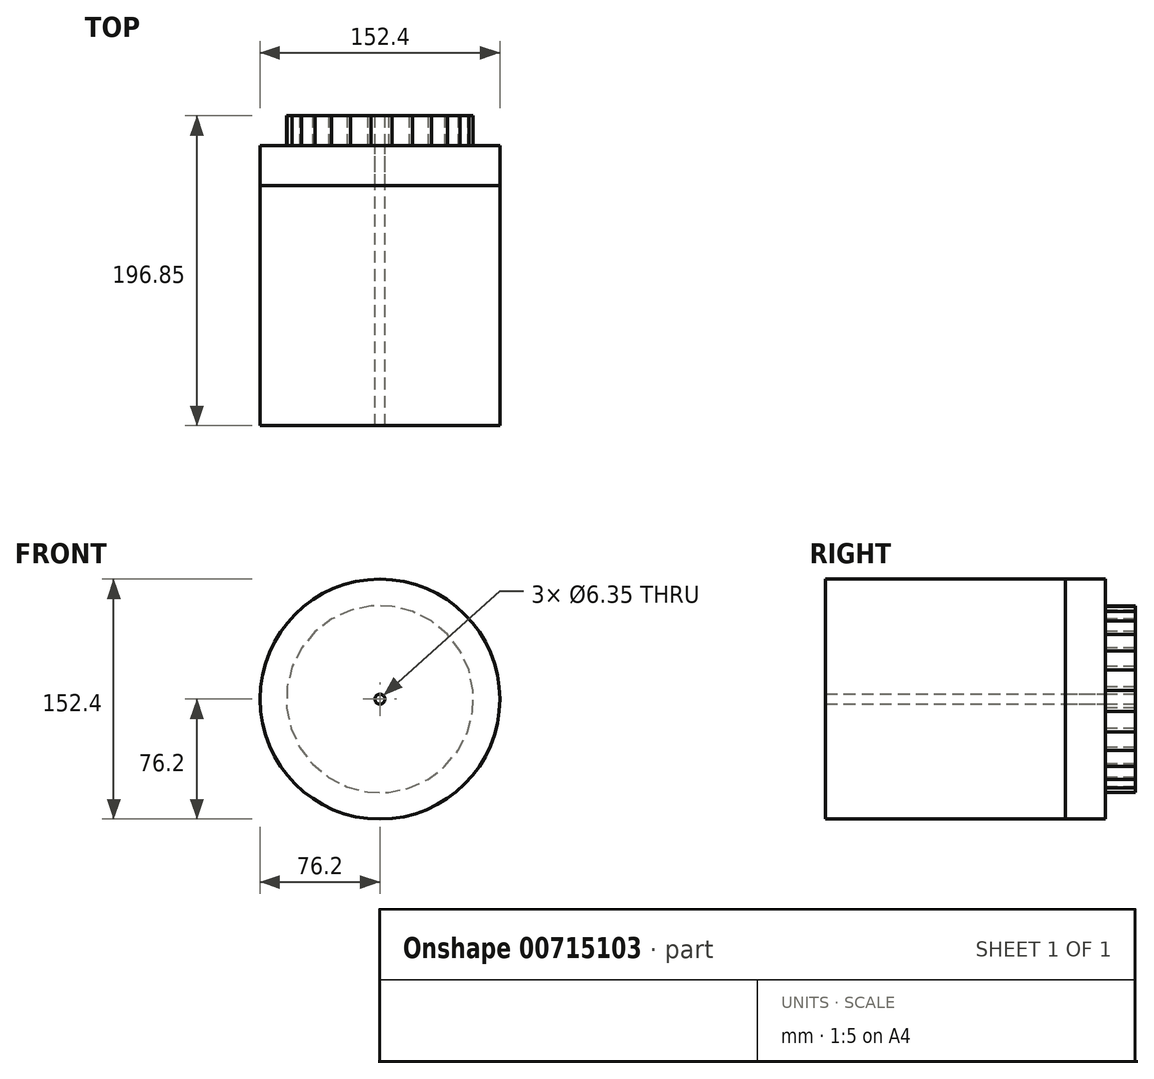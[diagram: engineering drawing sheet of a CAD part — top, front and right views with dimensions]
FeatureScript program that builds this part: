
annotation { "Feature Type Name" : "Feature", "Feature Type Description" : "" }
export const myFeature = defineFeature(function(context is Context, id is Id, definition is map)
    precondition{}
    {
        {
            var Q0;
            Q0=qCreatedBy(makeId("Front.planeOp"),FACE);
            var sketch = newSketch(context, id + "F0", { "sketchPlane" : qUnion([Q0])});
            skCircle(sketch, "E0", {"center": v(0, 0) * mm, "radius": 76.2 * mm});
            skSolve(sketch);
        }
        {
            var Q0;
            Q0=makeQuery(id+"F0.imprint","IMPRINT",FACE,{"disambiguationData":[TD([[makeQuery(id+"F0.imprint","IMPRINT",EDGE,{"derivedFrom":sQuery(id+"F0.wireOp",EDGE,"E0")}),1.0]])]});
            var sketch = newSketch(context, id + "F1", { "sketchPlane" : qUnion([Q0])});
            skSolve(sketch);
        }
        {
            var Q0;
            Q0=makeQuery(id+"F0.imprint","IMPRINT",FACE,{"disambiguationData":[TD([[makeQuery(id+"F0.imprint","IMPRINT",EDGE,{"derivedFrom":sQuery(id+"F0.wireOp",EDGE,"E0")}),1.0]])]});
            extrude(context, id + "F2", {"entities" : qUnion([Q0]), "depth" : 177.8 * mm, "offsetDistance" : 25.4 * mm});
        }
        {
            var Q0;
            Q0=makeQuery(id+"F1.imprint","IMPRINT",FACE,{"disambiguationData":[TD([[makeQuery(id+"F1.imprint","IMPRINT",EDGE,{"derivedFrom":makeQuery(id+"F0.imprint","IMPRINT",EDGE,{"derivedFrom":sQuery(id+"F0.wireOp",EDGE,"E0")})}),1.0]])]});
            extrude(context, id + "F3", {"entities" : qUnion([Q0]), "depth" : 25.4 * mm, "offsetDistance" : 25.4 * mm});
        }
        {
            var Q0;
            Q0=makeQuery(id+"F2.opExtrude","CAP_FACE",FACE,{"disambiguationData":[OSD([sQuery(id+"F0.wireOp",EDGE,"E0")])],"isStart":true});
            var sketch = newSketch(context, id + "F4", { "sketchPlane" : qUnion([Q0])});
            skCircle(sketch, "E1.cCircle", {"center": v(0, 0) * mm, "radius": 59.07 * mm, "construction": true});
            skLineSegment(sketch, "E1.0", {"start": v(41.18, 42.87) * mm, "end": v(49.69, 32.63) * mm});
            skLineSegment(sketch, "E1.1", {"start": v(49.69, 32.63) * mm, "end": v(55.7, 20.76) * mm});
            skLineSegment(sketch, "E1.2", {"start": v(55.7, 20.76) * mm, "end": v(58.93, 7.84) * mm});
            skLineSegment(sketch, "E1.3", {"start": v(58.93, 7.84) * mm, "end": v(59.2, -5.47) * mm});
            skLineSegment(sketch, "E1.4", {"start": v(59.2, -5.47) * mm, "end": v(56.5, -18.5) * mm});
            skLineSegment(sketch, "E1.5", {"start": v(56.5, -18.5) * mm, "end": v(50.96, -30.6) * mm});
            skLineSegment(sketch, "E1.6", {"start": v(50.96, -30.6) * mm, "end": v(42.87, -41.18) * mm});
            skLineSegment(sketch, "E1.7", {"start": v(42.87, -41.18) * mm, "end": v(32.63, -49.69) * mm});
            skLineSegment(sketch, "E1.8", {"start": v(32.63, -49.69) * mm, "end": v(20.76, -55.7) * mm});
            skLineSegment(sketch, "E1.9", {"start": v(20.76, -55.7) * mm, "end": v(7.84, -58.93) * mm});
            skLineSegment(sketch, "E1.10", {"start": v(7.84, -58.93) * mm, "end": v(-5.47, -59.2) * mm});
            skLineSegment(sketch, "E1.11", {"start": v(-5.47, -59.2) * mm, "end": v(-18.5, -56.5) * mm});
            skLineSegment(sketch, "E1.12", {"start": v(-18.5, -56.5) * mm, "end": v(-30.6, -50.96) * mm});
            skLineSegment(sketch, "E1.13", {"start": v(-30.6, -50.96) * mm, "end": v(-41.18, -42.87) * mm});
            skLineSegment(sketch, "E1.14", {"start": v(-41.18, -42.87) * mm, "end": v(-49.69, -32.63) * mm});
            skLineSegment(sketch, "E1.15", {"start": v(-49.69, -32.63) * mm, "end": v(-55.7, -20.76) * mm});
            skLineSegment(sketch, "E1.16", {"start": v(-55.7, -20.76) * mm, "end": v(-58.93, -7.84) * mm});
            skLineSegment(sketch, "E1.17", {"start": v(-58.93, -7.84) * mm, "end": v(-59.2, 5.47) * mm});
            skLineSegment(sketch, "E1.18", {"start": v(-59.2, 5.47) * mm, "end": v(-56.5, 18.5) * mm});
            skLineSegment(sketch, "E1.19", {"start": v(-56.5, 18.5) * mm, "end": v(-50.96, 30.6) * mm});
            skLineSegment(sketch, "E1.20", {"start": v(-50.96, 30.6) * mm, "end": v(-42.87, 41.18) * mm});
            skLineSegment(sketch, "E1.21", {"start": v(-42.87, 41.18) * mm, "end": v(-32.63, 49.69) * mm});
            skLineSegment(sketch, "E1.22", {"start": v(-32.63, 49.69) * mm, "end": v(-20.76, 55.7) * mm});
            skLineSegment(sketch, "E1.23", {"start": v(-20.76, 55.7) * mm, "end": v(-7.84, 58.93) * mm});
            skLineSegment(sketch, "E1.24", {"start": v(-7.84, 58.93) * mm, "end": v(5.47, 59.2) * mm});
            skLineSegment(sketch, "E1.25", {"start": v(5.47, 59.2) * mm, "end": v(18.5, 56.5) * mm});
            skLineSegment(sketch, "E1.26", {"start": v(18.5, 56.5) * mm, "end": v(30.6, 50.96) * mm});
            skLineSegment(sketch, "E1.27", {"start": v(30.6, 50.96) * mm, "end": v(41.18, 42.87) * mm});
            skPoint(sketch, "E1.0.midPoint", {"position": v(45.44, 37.75) * mm});
            skSolve(sketch);
        }
        {
            var Q0;
            Q0=makeQuery(id+"F4.imprint","IMPRINT",FACE,{"disambiguationData":[TD([[makeQuery(id+"F4.imprint","IMPRINT",EDGE,{"derivedFrom":sQuery(id+"F4.wireOp",EDGE,"E1.0")}),-1.0]])]});
            extrude(context, id + "F5", {"entities" : qUnion([Q0]), "depth" : 19.05 * mm, "offsetDistance" : 25.4 * mm});
        }
        {
            var Q0;
            Q0=makeQuery(id+"F5.opExtrude","CAP_FACE",FACE,{"disambiguationData":[OSD([sQuery(id+"F4.wireOp",EDGE,"E1.0"),sQuery(id+"F4.wireOp",EDGE,"E1.1"),sQuery(id+"F4.wireOp",EDGE,"E1.2"),sQuery(id+"F4.wireOp",EDGE,"E1.3"),sQuery(id+"F4.wireOp",EDGE,"E1.4"),sQuery(id+"F4.wireOp",EDGE,"E1.5"),sQuery(id+"F4.wireOp",EDGE,"E1.6"),sQuery(id+"F4.wireOp",EDGE,"E1.7"),sQuery(id+"F4.wireOp",EDGE,"E1.8"),sQuery(id+"F4.wireOp",EDGE,"E1.9"),sQuery(id+"F4.wireOp",EDGE,"E1.10"),sQuery(id+"F4.wireOp",EDGE,"E1.11"),sQuery(id+"F4.wireOp",EDGE,"E1.12"),sQuery(id+"F4.wireOp",EDGE,"E1.13"),sQuery(id+"F4.wireOp",EDGE,"E1.14"),sQuery(id+"F4.wireOp",EDGE,"E1.15"),sQuery(id+"F4.wireOp",EDGE,"E1.16"),sQuery(id+"F4.wireOp",EDGE,"E1.17"),sQuery(id+"F4.wireOp",EDGE,"E1.18"),sQuery(id+"F4.wireOp",EDGE,"E1.19"),sQuery(id+"F4.wireOp",EDGE,"E1.20"),sQuery(id+"F4.wireOp",EDGE,"E1.21"),sQuery(id+"F4.wireOp",EDGE,"E1.22"),sQuery(id+"F4.wireOp",EDGE,"E1.23"),sQuery(id+"F4.wireOp",EDGE,"E1.24"),sQuery(id+"F4.wireOp",EDGE,"E1.25"),sQuery(id+"F4.wireOp",EDGE,"E1.26"),sQuery(id+"F4.wireOp",EDGE,"E1.27")])],"isStart":false});
            var sketch = newSketch(context, id + "F6", { "sketchPlane" : qUnion([Q0])});
            skCircle(sketch, "E2", {"center": v(0, 0) * mm, "radius": 12.87 * mm});
            skSolve(sketch);
        }
        {
            var Q0;
            Q0=sQuery(id+"F6.wireOp",EDGE,"E2");
            extrude(context, id + "F7", {"bodyType" : ToolBodyType.SURFACE, "surfaceEntities" : qUnion([Q0]), "depth" : 1.27 * mm, "offsetDistance" : 25.4 * mm});
        }
        {
            var Q0;
            Q0=makeQuery(id+"F5.opExtrude","CAP_FACE",FACE,{"disambiguationData":[OSD([sQuery(id+"F4.wireOp",EDGE,"E1.0"),sQuery(id+"F4.wireOp",EDGE,"E1.1"),sQuery(id+"F4.wireOp",EDGE,"E1.2"),sQuery(id+"F4.wireOp",EDGE,"E1.3"),sQuery(id+"F4.wireOp",EDGE,"E1.4"),sQuery(id+"F4.wireOp",EDGE,"E1.5"),sQuery(id+"F4.wireOp",EDGE,"E1.6"),sQuery(id+"F4.wireOp",EDGE,"E1.7"),sQuery(id+"F4.wireOp",EDGE,"E1.8"),sQuery(id+"F4.wireOp",EDGE,"E1.9"),sQuery(id+"F4.wireOp",EDGE,"E1.10"),sQuery(id+"F4.wireOp",EDGE,"E1.11"),sQuery(id+"F4.wireOp",EDGE,"E1.12"),sQuery(id+"F4.wireOp",EDGE,"E1.13"),sQuery(id+"F4.wireOp",EDGE,"E1.14"),sQuery(id+"F4.wireOp",EDGE,"E1.15"),sQuery(id+"F4.wireOp",EDGE,"E1.16"),sQuery(id+"F4.wireOp",EDGE,"E1.17"),sQuery(id+"F4.wireOp",EDGE,"E1.18"),sQuery(id+"F4.wireOp",EDGE,"E1.19"),sQuery(id+"F4.wireOp",EDGE,"E1.20"),sQuery(id+"F4.wireOp",EDGE,"E1.21"),sQuery(id+"F4.wireOp",EDGE,"E1.22"),sQuery(id+"F4.wireOp",EDGE,"E1.23"),sQuery(id+"F4.wireOp",EDGE,"E1.24"),sQuery(id+"F4.wireOp",EDGE,"E1.25"),sQuery(id+"F4.wireOp",EDGE,"E1.26"),sQuery(id+"F4.wireOp",EDGE,"E1.27")])],"isStart":false});
            var sketch = newSketch(context, id + "F8", { "sketchPlane" : qUnion([Q0])});
            skPoint(sketch, "E3", {"position": v(0, 0) * mm});
            skSolve(sketch);
        }
        {
            var Q0;
            Q0=sQuery(id+"F8.wireOp",VERTEX,"E3");
            var Q1;
            Q1=makeQuery(id+"F2.opExtrude","SWEPT_BODY",BODY,{"disambiguationData":[OSD([sQuery(id+"F0.wireOp",EDGE,"E0")])]});
            var Q2;
            Q2=makeQuery(id+"F3.opExtrude","SWEPT_BODY",BODY,{"disambiguationData":[OSD([sQuery(id+"F0.wireOp",EDGE,"E0")])]});
            var Q3;
            Q3=makeQuery(id+"F5.opExtrude","SWEPT_BODY",BODY,{"disambiguationData":[OSD([sQuery(id+"F4.wireOp",EDGE,"E1.0"),sQuery(id+"F4.wireOp",EDGE,"E1.1"),sQuery(id+"F4.wireOp",EDGE,"E1.2"),sQuery(id+"F4.wireOp",EDGE,"E1.3"),sQuery(id+"F4.wireOp",EDGE,"E1.4"),sQuery(id+"F4.wireOp",EDGE,"E1.5"),sQuery(id+"F4.wireOp",EDGE,"E1.6"),sQuery(id+"F4.wireOp",EDGE,"E1.7"),sQuery(id+"F4.wireOp",EDGE,"E1.8"),sQuery(id+"F4.wireOp",EDGE,"E1.9"),sQuery(id+"F4.wireOp",EDGE,"E1.10"),sQuery(id+"F4.wireOp",EDGE,"E1.11"),sQuery(id+"F4.wireOp",EDGE,"E1.12"),sQuery(id+"F4.wireOp",EDGE,"E1.13"),sQuery(id+"F4.wireOp",EDGE,"E1.14"),sQuery(id+"F4.wireOp",EDGE,"E1.15"),sQuery(id+"F4.wireOp",EDGE,"E1.16"),sQuery(id+"F4.wireOp",EDGE,"E1.17"),sQuery(id+"F4.wireOp",EDGE,"E1.18"),sQuery(id+"F4.wireOp",EDGE,"E1.19"),sQuery(id+"F4.wireOp",EDGE,"E1.20"),sQuery(id+"F4.wireOp",EDGE,"E1.21"),sQuery(id+"F4.wireOp",EDGE,"E1.22"),sQuery(id+"F4.wireOp",EDGE,"E1.23"),sQuery(id+"F4.wireOp",EDGE,"E1.24"),sQuery(id+"F4.wireOp",EDGE,"E1.25"),sQuery(id+"F4.wireOp",EDGE,"E1.26"),sQuery(id+"F4.wireOp",EDGE,"E1.27")])]});
            hole(context, id + "F9", {"style" : HoleStyle.SIMPLE, "endStyle" : HoleEndStyle.THROUGH, "holeDiameter" : 6.35 * mm, "majorDiameter" : 6.35 * mm, "isTappedThrough" : true, "tappedDepth" : 12.7 * mm, "tapClearance" : 3, "locations" : qUnion([Q0]), "scope" : qUnion([Q1, Q2, Q3])});
        }
    });
